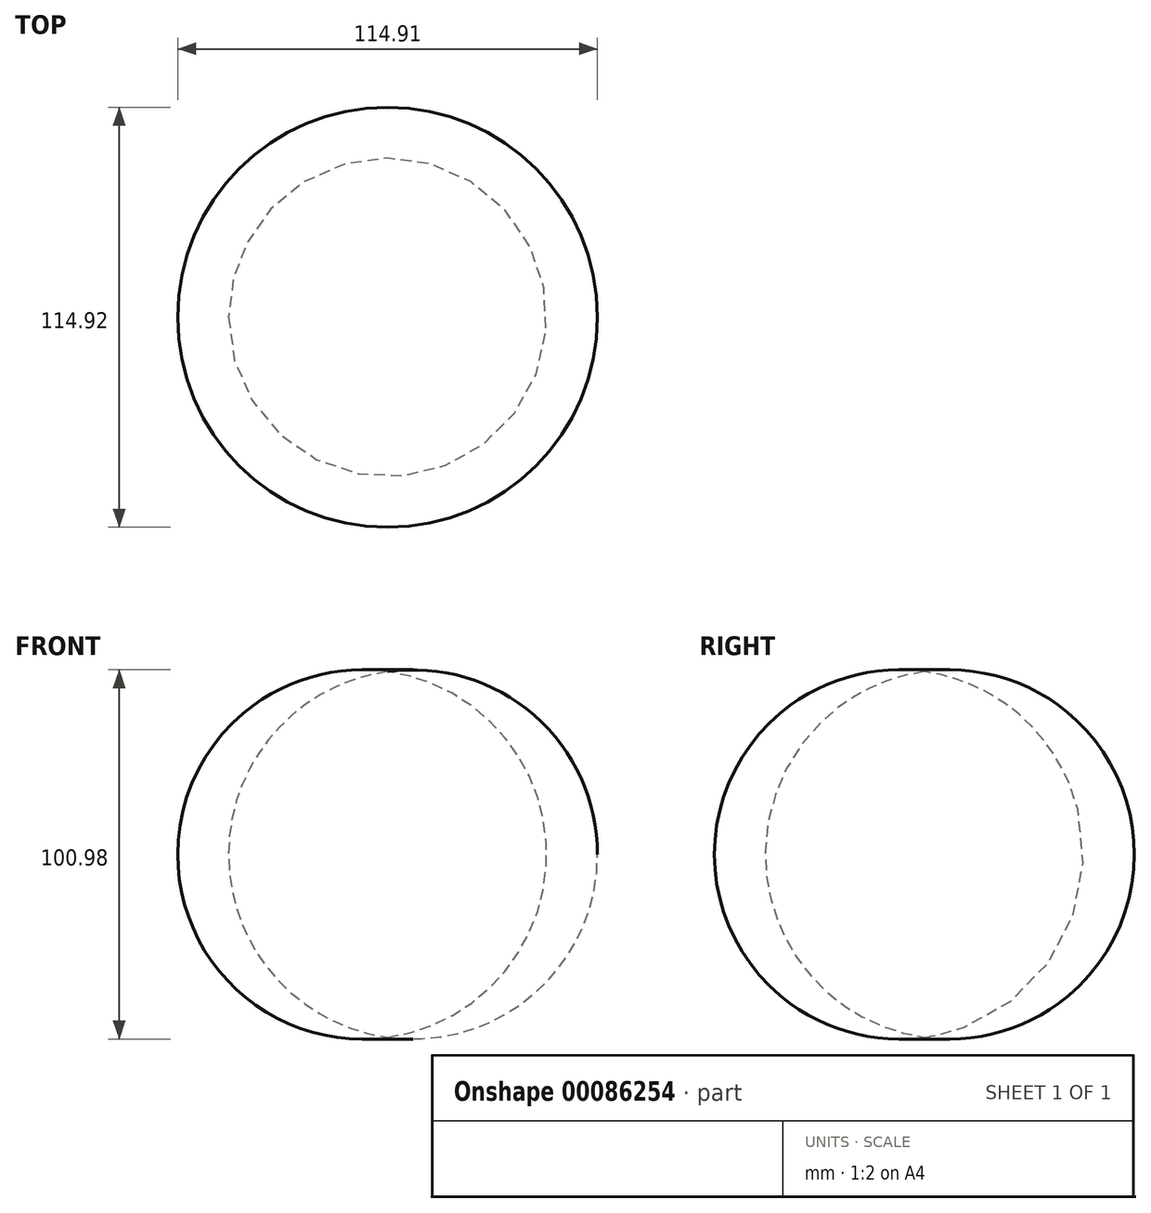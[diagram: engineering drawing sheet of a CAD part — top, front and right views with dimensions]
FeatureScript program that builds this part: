
annotation { "Feature Type Name" : "Feature", "Feature Type Description" : "" }
export const myFeature = defineFeature(function(context is Context, id is Id, definition is map)
    precondition{}
    {
        {
            var Q0;
            Q0=qCreatedBy(makeId("Front.planeOp"),FACE);
            var sketch = newSketch(context, id + "F0", { "sketchPlane" : qUnion([Q0])});
            skLineSegment(sketch, "E0", {"start": v(-42.58, 58) * mm, "end": v(-42.58, -42) * mm});
            skArc(sketch, "E1", {"start": v(-42.58, -42) * mm, "mid": v(14.88, 8) * mm, "end": v(-42.58, 58) * mm});
            skSolve(sketch);
        }
        {
            var Q0;
            Q0=makeQuery(id+"F0.imprint","IMPRINT",FACE,{"disambiguationData":[TD([[makeQuery(id+"F0.imprint","IMPRINT",EDGE,{"derivedFrom":sQuery(id+"F0.wireOp",EDGE,"E0")}),1.0]])]});
            var sketch = newSketch(context, id + "F1", { "sketchPlane" : qUnion([Q0])});
            skSolve(sketch);
        }
        {
            var Q0;
            Q0 = qSketchRegion(id + "F1", true);
            var Q1;
            Q1=makeQuery(id+"F0.imprint","IMPRINT",FACE,{"disambiguationData":[TD([[makeQuery(id+"F0.imprint","IMPRINT",EDGE,{"derivedFrom":sQuery(id+"F0.wireOp",EDGE,"E0")}),1.0]])]});
            var Q2;
            Q2=sQuery(id+"F0.wireOp",EDGE,"E0");
            revolve(context, id + "F2", {"entities" : qUnion([Q0, Q1]), "axis" : qUnion([Q2]), "revolveType" : RevolveType.FULL});
        }
    });
